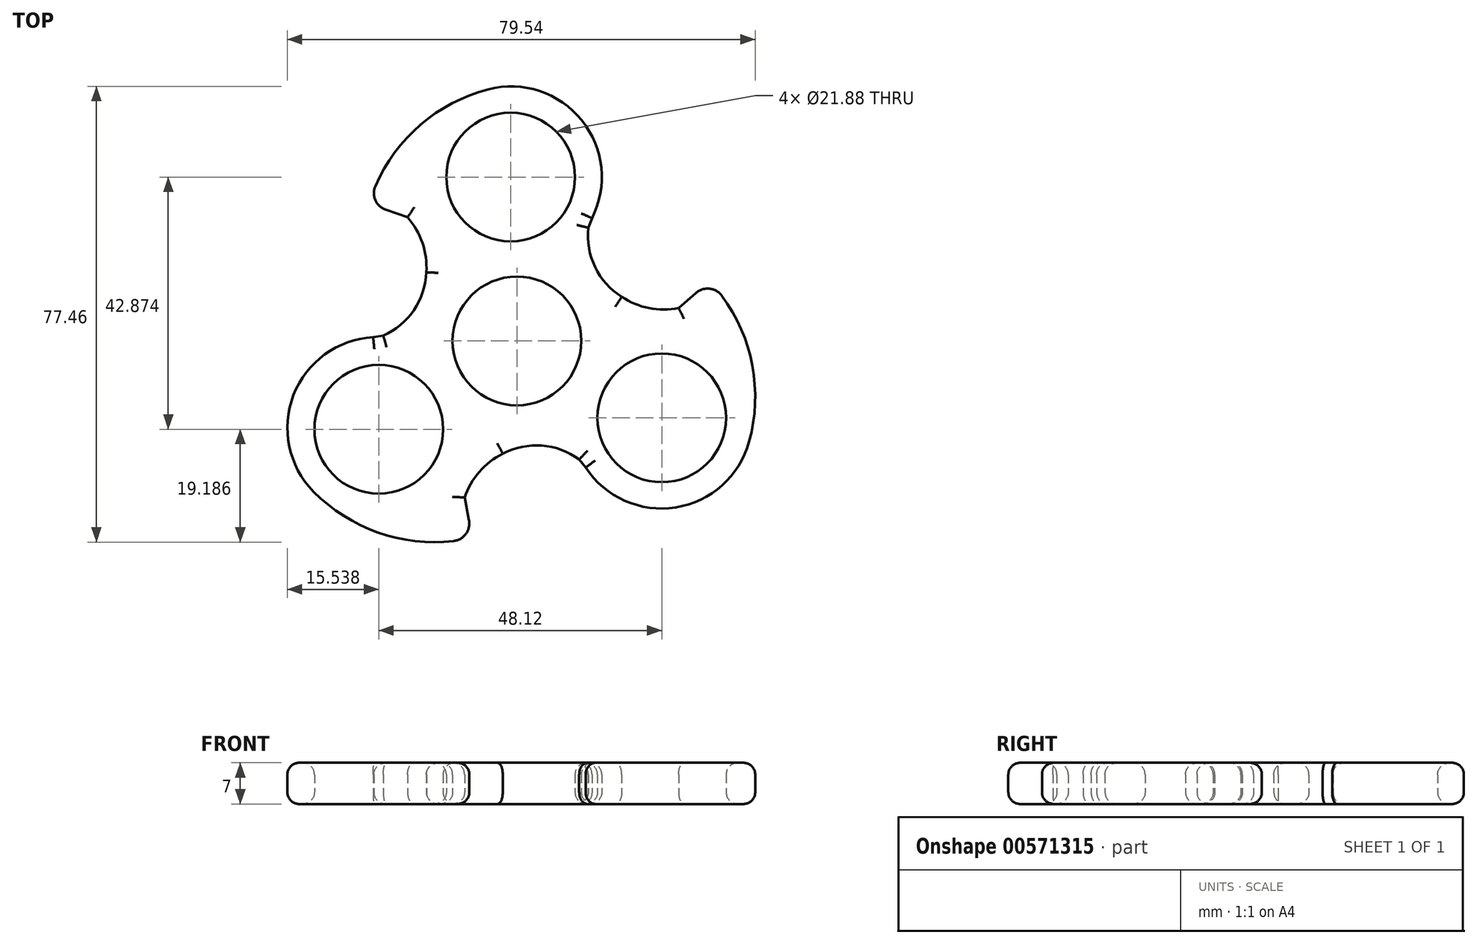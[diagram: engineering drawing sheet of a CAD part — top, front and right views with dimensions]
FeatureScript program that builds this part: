
annotation { "Feature Type Name" : "Feature", "Feature Type Description" : "" }
export const myFeature = defineFeature(function(context is Context, id is Id, definition is map)
    precondition{}
    {
        {
            var Q0;
            Q0=qCreatedBy(makeId("Top.planeOp"),FACE);
            var sketch = newSketch(context, id + "F0", { "sketchPlane" : qUnion([Q0])});
            skCircle(sketch, "E0", {"center": v(0, 0) * mm, "radius": 10.94 * mm});
            skCircle(sketch, "E1", {"center": v(-1.07, 27.86) * mm, "radius": 10.94 * mm});
            skCircle(sketch, "E2.1.0", {"center": v(-23.5, -15.01) * mm, "radius": 10.94 * mm});
            skCircle(sketch, "E2.2.0", {"center": v(24.63, -13.07) * mm, "radius": 10.94 * mm});
            skPoint(sketch, "E3.start.orphan", {"position": v(0, 43.22) * mm});
            skLineSegment(sketch, "E4.2.0", {"start": v(-18.6, 21.01) * mm, "end": v(-25.2, 23.3) * mm});
            skArc(sketch, "E5.1.3", {"start": v(-22.73, 0.9) * mm, "mid": v(-17.52, 5.23) * mm, "end": v(-15.4, 11.68) * mm});
            skArc(sketch, "E5.2.0", {"start": v(12.77, 20.87) * mm, "mid": v(11.01, 37.51) * mm, "end": v(-4.88, 42.76) * mm});
            skArc(sketch, "E5.2.1", {"start": v(-4.88, 42.76) * mm, "mid": v(-17.57, 35.67) * mm, "end": v(-25.2, 23.3) * mm});
            skArc(sketch, "E6", {"start": v(-15.4, 11.68) * mm, "mid": v(-16.06, 16.66) * mm, "end": v(-18.6, 21.01) * mm});
            skPoint(sketch, "E7.orphan", {"position": v(12.21, 19.87) * mm});
            skPoint(sketch, "E8.2.0.end.orphan", {"position": v(32.77, 10.17) * mm});
            skPoint(sketch, "E9.orphan", {"position": v(11.13, -20.54) * mm});
            skPoint(sketch, "E10.trimOffspring.end.orphan", {"position": v(27.48, 5.59) * mm});
            skArc(sketch, "E11", {"start": v(-24.47, 0.63) * mm, "mid": v(-24.45, 0.63) * mm, "end": v(-24.43, 0.63) * mm});
            skLineSegment(sketch, "E12", {"start": v(-8.87, -26.5) * mm, "end": v(-8.87, -26.6) * mm});
            skPoint(sketch, "E13.orphan", {"position": v(-8.9, -26.47) * mm});
            skLineSegment(sketch, "E14", {"start": v(27.5, 5.57) * mm, "end": v(27.59, 5.63) * mm});
            skLineSegment(sketch, "E15", {"start": v(12.77, 20.87) * mm, "end": v(12.76, 20.84) * mm});
            skPoint(sketch, "E16.1.2.end.orphan", {"position": v(-7.57, -33.47) * mm});
            skLineSegment(sketch, "E17.1.1", {"start": v(-24.46, 0.62) * mm, "end": v(-22.73, 0.9) * mm});
            skArc(sketch, "E17.1.2", {"start": v(-7.58, -33.47) * mm, "mid": v(-7.57, -33.47) * mm, "end": v(-7.57, -33.47) * mm});
            skLineSegment(sketch, "E17.1.3", {"start": v(-7.58, -33.47) * mm, "end": v(-7.57, -33.48) * mm});
            skArc(sketch, "E17.1.4", {"start": v(-8.87, -26.51) * mm, "mid": v(-8.88, -26.56) * mm, "end": v(-8.9, -26.6) * mm});
            skArc(sketch, "E17.1.6", {"start": v(11.69, -21.5) * mm, "mid": v(11.68, -21.49) * mm, "end": v(11.67, -21.47) * mm});
            skLineSegment(sketch, "E17.2.1", {"start": v(11.69, -21.5) * mm, "end": v(11.67, -21.47) * mm});
            skArc(sketch, "E17.2.2", {"start": v(32.77, 10.17) * mm, "mid": v(32.77, 10.17) * mm, "end": v(32.77, 10.17) * mm});
            skLineSegment(sketch, "E17.2.3", {"start": v(32.77, 10.17) * mm, "end": v(32.78, 10.18) * mm});
            skArc(sketch, "E17.2.5", {"start": v(12.2, 19.69) * mm, "mid": v(12.17, 19.46) * mm, "end": v(12.14, 19.24) * mm});
            skPoint(sketch, "E18.orphan", {"position": v(12.14, 19.24) * mm});
            skPoint(sketch, "E19.orphan", {"position": v(12.78, 20.88) * mm});
            skLineSegment(sketch, "E20", {"start": v(12.76, 20.84) * mm, "end": v(12.2, 19.69) * mm});
            skPoint(sketch, "E21.orphan", {"position": v(12.23, 19.88) * mm});
            skPoint(sketch, "E22.orphan", {"position": v(-34.6, -25.6) * mm});
            skPoint(sketch, "E23.orphan", {"position": v(-2.41, -19.18) * mm});
            skPoint(sketch, "E24.orphan", {"position": v(11.1, -20.53) * mm});
            skPoint(sketch, "E25.orphan", {"position": v(39.47, -17.15) * mm});
            skPoint(sketch, "E26.orphan", {"position": v(17.81, 7.5) * mm});
            skPoint(sketch, "E27.orphan", {"position": v(-23.33, 0.65) * mm});
            skLineSegment(sketch, "E28.1.0", {"start": v(11.69, -21.5) * mm, "end": v(10.6, -20.13) * mm});
            skArc(sketch, "E28.1.1", {"start": v(10.6, -20.13) * mm, "mid": v(4.23, -17.79) * mm, "end": v(-2.41, -19.18) * mm});
            skArc(sketch, "E28.1.2", {"start": v(-2.41, -19.18) * mm, "mid": v(-6.4, -22.24) * mm, "end": v(-8.9, -26.6) * mm});
            skLineSegment(sketch, "E28.1.3", {"start": v(-8.9, -26.6) * mm, "end": v(-7.57, -33.48) * mm});
            skArc(sketch, "E28.1.4", {"start": v(-34.6, -25.6) * mm, "mid": v(-22.1, -33.05) * mm, "end": v(-7.57, -33.47) * mm});
            skArc(sketch, "E28.1.5", {"start": v(-24.46, 0.62) * mm, "mid": v(-38, -9.22) * mm, "end": v(-34.6, -25.6) * mm});
            skLineSegment(sketch, "E28.1.6", {"start": v(-24.43, 0.63) * mm, "end": v(-23.15, 0.72) * mm});
            skArc(sketch, "E28.1.7", {"start": v(-23.15, 0.72) * mm, "mid": v(-22.94, 0.8) * mm, "end": v(-22.73, 0.9) * mm});
            skLineSegment(sketch, "E28.2.0", {"start": v(12.77, 20.87) * mm, "end": v(12.14, 19.24) * mm});
            skArc(sketch, "E28.2.1", {"start": v(12.14, 19.24) * mm, "mid": v(13.3, 12.56) * mm, "end": v(17.81, 7.5) * mm});
            skArc(sketch, "E28.2.2", {"start": v(17.81, 7.5) * mm, "mid": v(22.46, 5.58) * mm, "end": v(27.5, 5.6) * mm});
            skLineSegment(sketch, "E28.2.3", {"start": v(27.5, 5.6) * mm, "end": v(32.78, 10.18) * mm});
            skArc(sketch, "E28.2.4", {"start": v(39.47, -17.15) * mm, "mid": v(39.68, -2.62) * mm, "end": v(32.77, 10.17) * mm});
            skArc(sketch, "E28.2.5", {"start": v(11.69, -21.5) * mm, "mid": v(26.98, -28.3) * mm, "end": v(39.47, -17.15) * mm});
            skLineSegment(sketch, "E28.2.6", {"start": v(11.67, -21.47) * mm, "end": v(10.95, -20.4) * mm});
            skArc(sketch, "E28.2.7", {"start": v(10.95, -20.4) * mm, "mid": v(10.77, -20.27) * mm, "end": v(10.6, -20.13) * mm});
            skSolve(sketch);
        }
        {
            var Q0;
            Q0 = qSketchRegion(id + "F0", true);
            extrude(context, id + "F1", {"entities" : qUnion([Q0]), "depth" : 7 * mm, "offsetDistance" : 25 * mm});
        }
        {
            var Q0;
            Q0=makeQuery(id+"F1.opExtrude","CAP_FACE",FACE,{"disambiguationData":[OSD([sQuery(id+"F0.wireOp",EDGE,"E0"),sQuery(id+"F0.wireOp",EDGE,"E1"),sQuery(id+"F0.wireOp",EDGE,"E2.1.0"),sQuery(id+"F0.wireOp",EDGE,"E2.2.0"),sQuery(id+"F0.wireOp",EDGE,"E4.2.0"),sQuery(id+"F0.wireOp",EDGE,"E5.1.3"),sQuery(id+"F0.wireOp",EDGE,"E5.2.0"),sQuery(id+"F0.wireOp",EDGE,"E5.2.1"),sQuery(id+"F0.wireOp",EDGE,"E6"),sQuery(id+"F0.wireOp",EDGE,"E16.1.0"),sQuery(id+"F0.wireOp",EDGE,"E16.1.1"),sQuery(id+"F0.wireOp",EDGE,"E16.1.2"),sQuery(id+"F0.wireOp",EDGE,"E16.1.3"),sQuery(id+"F0.wireOp",EDGE,"E16.1.4"),sQuery(id+"F0.wireOp",EDGE,"E16.2.0"),sQuery(id+"F0.wireOp",EDGE,"E16.2.1"),sQuery(id+"F0.wireOp",EDGE,"E16.2.2"),sQuery(id+"F0.wireOp",EDGE,"E16.2.3"),sQuery(id+"F0.wireOp",EDGE,"E16.2.4"),sQuery(id+"F0.wireOp",EDGE,"yAPYmcU9-OE8H-p4wC-JMIL-CkxSXegamixB"),sQuery(id+"F0.wireOp",EDGE,"E11"),sQuery(id+"F0.wireOp",EDGE,"AGjoT7fz-NzXp-PSp4-SgIZ-bJBbMCs8cf8k"),sQuery(id+"F0.wireOp",EDGE,"E12"),sQuery(id+"F0.wireOp",EDGE,"E14")])],"isStart":false});
            var Q1;
            Q1=makeQuery(id+"F1.opExtrude","CAP_FACE",FACE,{"disambiguationData":[OSD([sQuery(id+"F0.wireOp",EDGE,"E0"),sQuery(id+"F0.wireOp",EDGE,"E1"),sQuery(id+"F0.wireOp",EDGE,"E2.1.0"),sQuery(id+"F0.wireOp",EDGE,"E2.2.0"),sQuery(id+"F0.wireOp",EDGE,"E4.2.0"),sQuery(id+"F0.wireOp",EDGE,"E5.1.3"),sQuery(id+"F0.wireOp",EDGE,"E5.2.0"),sQuery(id+"F0.wireOp",EDGE,"E5.2.1"),sQuery(id+"F0.wireOp",EDGE,"E6"),sQuery(id+"F0.wireOp",EDGE,"E16.1.0"),sQuery(id+"F0.wireOp",EDGE,"E16.1.1"),sQuery(id+"F0.wireOp",EDGE,"E16.1.2"),sQuery(id+"F0.wireOp",EDGE,"E16.1.3"),sQuery(id+"F0.wireOp",EDGE,"E16.1.4"),sQuery(id+"F0.wireOp",EDGE,"E16.2.0"),sQuery(id+"F0.wireOp",EDGE,"E16.2.1"),sQuery(id+"F0.wireOp",EDGE,"E16.2.2"),sQuery(id+"F0.wireOp",EDGE,"E16.2.3"),sQuery(id+"F0.wireOp",EDGE,"E16.2.4"),sQuery(id+"F0.wireOp",EDGE,"yAPYmcU9-OE8H-p4wC-JMIL-CkxSXegamixB"),sQuery(id+"F0.wireOp",EDGE,"E11"),sQuery(id+"F0.wireOp",EDGE,"AGjoT7fz-NzXp-PSp4-SgIZ-bJBbMCs8cf8k"),sQuery(id+"F0.wireOp",EDGE,"E12"),sQuery(id+"F0.wireOp",EDGE,"E14")])],"isStart":true});
            fillet(context, id + "F2", {"entities" : qUnion([Q0, Q1]), "radius" : 2 * mm, "tangentPropagation" : true, "allowEdgeOverflow" : false});
        }
        {
            var Q0;
            Q0=makeQuery(id+"F1.opExtrude","SWEPT_EDGE",EDGE,{"disambiguationData":[OSD([sQuery(id+"F0.wireOp",EDGE,"E4.2.0"),sQuery(id+"F0.wireOp",EDGE,"E5.2.1")])]});
            var Q1;
            Q1=makeQuery(id+"F1.opExtrude","SWEPT_EDGE",EDGE,{"disambiguationData":[OSD([sQuery(id+"F0.wireOp",EDGE,"E16.1.2"),sQuery(id+"F0.wireOp",EDGE,"E16.1.3")])]});
            var Q2;
            Q2=makeQuery(id+"F1.opExtrude","SWEPT_EDGE",EDGE,{"disambiguationData":[OSD([sQuery(id+"F0.wireOp",EDGE,"E16.2.2"),sQuery(id+"F0.wireOp",EDGE,"E16.2.3")])]});
            var Q3;
            Q3=makeQuery(id+"F1.opExtrude","SWEPT_EDGE",EDGE,{"disambiguationData":[OSD([sQuery(id+"F0.wireOp",EDGE,"E28.1.3"),sQuery(id+"F0.wireOp",EDGE,"E28.1.4")])]});
            var Q4;
            Q4=makeQuery(id+"F1.opExtrude","SWEPT_EDGE",EDGE,{"disambiguationData":[OSD([sQuery(id+"F0.wireOp",EDGE,"E28.2.3"),sQuery(id+"F0.wireOp",EDGE,"E28.2.4")])]});
            fillet(context, id + "F3", {"entities" : qUnion([Q0, Q1, Q2, Q3, Q4]), "radius" : 3 * mm, "tangentPropagation" : true, "allowEdgeOverflow" : false});
        }
    });
